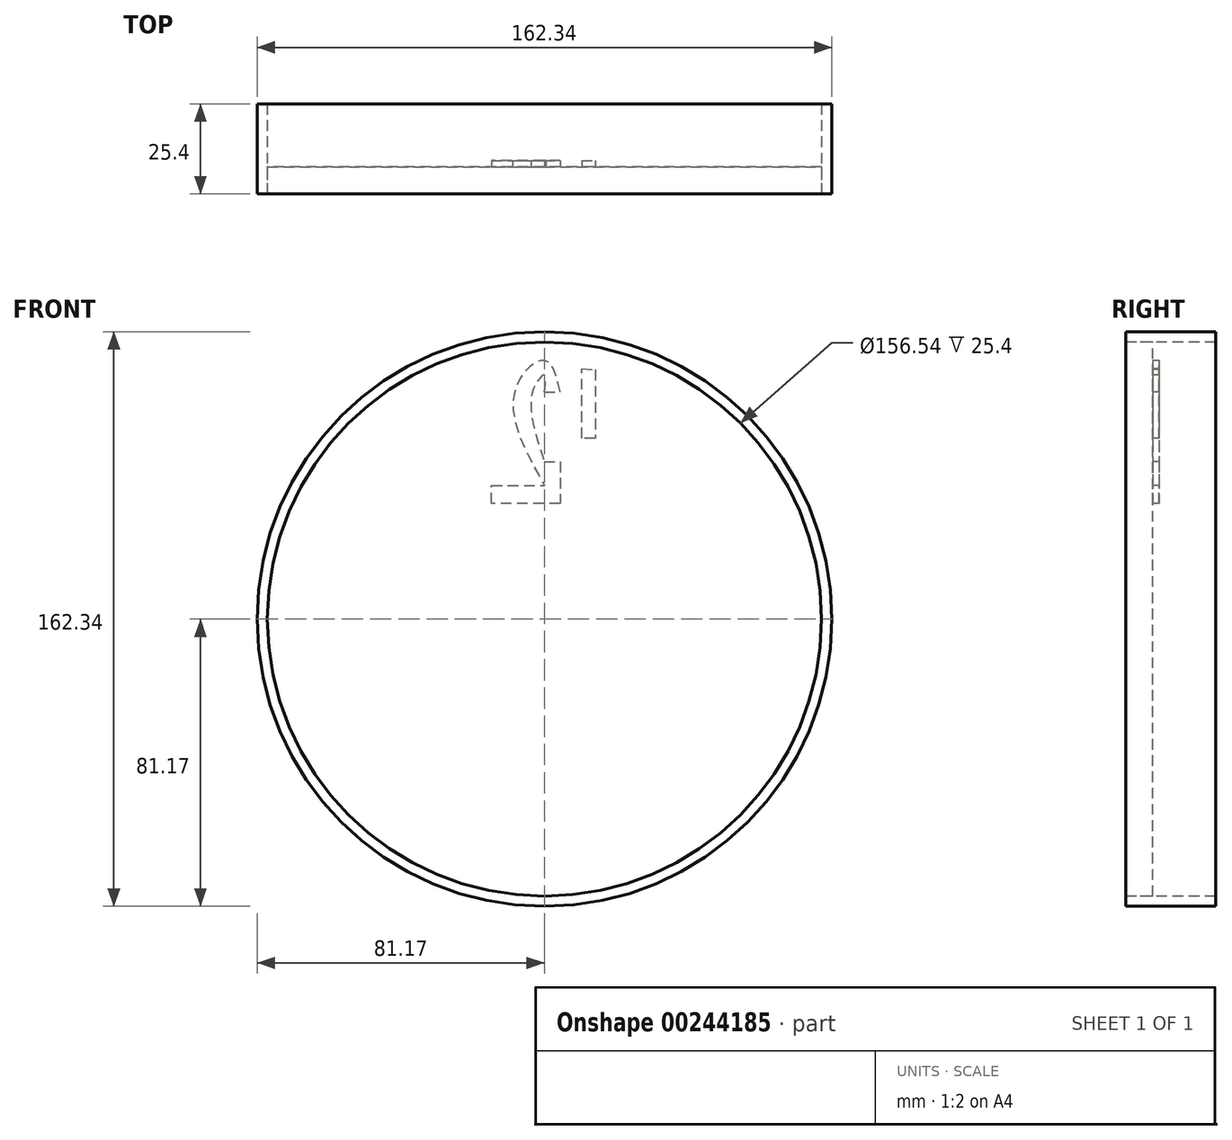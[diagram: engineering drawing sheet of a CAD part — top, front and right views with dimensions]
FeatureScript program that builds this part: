
annotation { "Feature Type Name" : "Feature", "Feature Type Description" : "" }
export const myFeature = defineFeature(function(context is Context, id is Id, definition is map)
    precondition{}
    {
        {
            var Q0;
            Q0=qCreatedBy(makeId("Front.planeOp"),FACE);
            var sketch = newSketch(context, id + "F0", { "sketchPlane" : qUnion([Q0])});
            skCircle(sketch, "E0", {"center": v(0, 0) * mm, "radius": 81.17 * mm});
            skCircle(sketch, "E1", {"center": v(0, 0) * mm, "radius": 78.27 * mm});
            skSolve(sketch);
        }
        {
            var Q0;
            Q0=makeQuery(id+"F0.imprint","IMPRINT",FACE,{"disambiguationData":[TD([[makeQuery(id+"F0.imprint","IMPRINT",EDGE,{"derivedFrom":sQuery(id+"F0.wireOp",EDGE,"E0")}),1.0]])]});
            extrude(context, id + "F1", {"entities" : qUnion([Q0]), "oppositeDirection" : true, "depth" : 25.4 * mm});
        }
        {
            var Q0;
            Q0=makeQuery(id+"F0.imprint","IMPRINT",FACE,{"disambiguationData":[TD([[makeQuery(id+"F0.imprint","IMPRINT",EDGE,{"derivedFrom":sQuery(id+"F0.wireOp",EDGE,"E1")}),1.0]])]});
            extrude(context, id + "F2", {"entities" : qUnion([Q0]), "oppositeDirection" : true, "depth" : 7.62 * mm});
        }
        {
            var Q0;
            Q0=makeQuery(id+"F2.opExtrude","CAP_FACE",FACE,{"disambiguationData":[OSD([sQuery(id+"F0.wireOp",EDGE,"E1")])],"isStart":false});
            var sketch = newSketch(context, id + "F3", { "sketchPlane" : qUnion([Q0])});
            skLineSegment(sketch, "E2", {"start": v(-14.37, 70.46) * mm, "end": v(-14.37, 51.07) * mm});
            skLineSegment(sketch, "E3", {"start": v(-10.55, 51.07) * mm, "end": v(-10.55, 70.76) * mm});
            skLineSegment(sketch, "E4", {"start": v(-10.55, 70.76) * mm, "end": v(-14.37, 70.46) * mm});
            skLineSegment(sketch, "E5", {"start": v(-14.37, 51.07) * mm, "end": v(-10.55, 51.07) * mm});
            skLineSegment(sketch, "E6", {"start": v(0, 64.15) * mm, "end": v(-4.46, 64.15) * mm});
            skFitSpline(sketch, "E7", {"points": [v(-4.46, 64.15) * mm, v(0, 73.14) * mm, v(8.47, 64.15) * mm, v(0, 37.74) * mm], "startDerivative": vector(11.41, 48.57) * mm, "endDerivative": vector(-35.4, -63.84) * mm});
            skFitSpline(sketch, "E8", {"points": [v(0, 64.15) * mm, v(0, 68.92) * mm, v(3.4, 64.15) * mm, v(0, 44.48) * mm], "startDerivative": vector(-4.04, 28.25) * mm, "endDerivative": vector(-14.76, -44.07) * mm});
            skLineSegment(sketch, "E9", {"start": v(0, 44.48) * mm, "end": v(-4.46, 44.48) * mm});
            skLineSegment(sketch, "E10", {"start": v(-4.46, 44.48) * mm, "end": v(-4.46, 32.68) * mm});
            skLineSegment(sketch, "E11", {"start": v(-4.46, 32.68) * mm, "end": v(14.93, 32.68) * mm});
            skLineSegment(sketch, "E12", {"start": v(14.93, 32.68) * mm, "end": v(14.93, 37.74) * mm});
            skLineSegment(sketch, "E13", {"start": v(14.93, 37.74) * mm, "end": v(0, 37.74) * mm});
            skSolve(sketch);
        }
        {
            var Q0;
            Q0=makeQuery(id+"F3.imprint","IMPRINT",FACE,{"disambiguationData":[TD([[makeQuery(id+"F3.imprint","IMPRINT",EDGE,{"derivedFrom":sQuery(id+"F3.wireOp",EDGE,"E2")}),1.0]])]});
            var Q1;
            Q1=makeQuery(id+"F3.imprint","IMPRINT",FACE,{"disambiguationData":[TD([[makeQuery(id+"F3.imprint","IMPRINT",EDGE,{"derivedFrom":sQuery(id+"F3.wireOp",EDGE,"E6")}),-1.0]])]});
            extrude(context, id + "F4", {"entities" : qUnion([Q0, Q1]), "operationType" : NewBodyOperationType.ADD, "depth" : 1.78 * mm});
        }
    });
